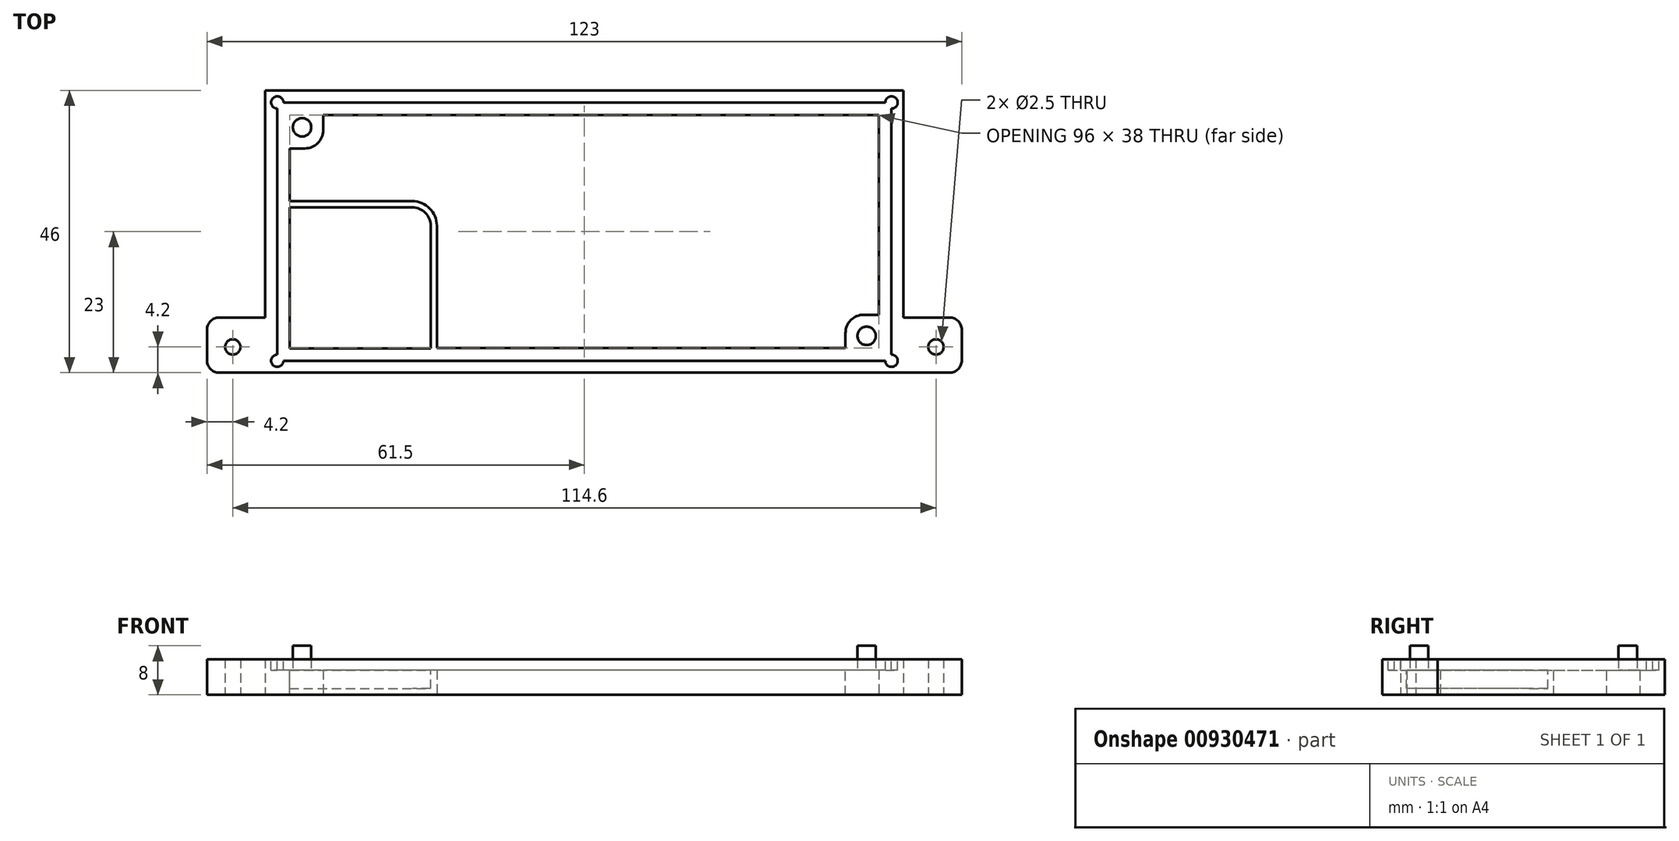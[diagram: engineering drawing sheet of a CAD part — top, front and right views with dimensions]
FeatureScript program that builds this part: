
annotation { "Feature Type Name" : "Feature", "Feature Type Description" : "" }
export const myFeature = defineFeature(function(context is Context, id is Id, definition is map)
    precondition{}
    {
        {
            var Q0;
            Q0=qCreatedBy(makeId("Top.planeOp"),FACE);
            var sketch = newSketch(context, id + "F0", { "sketchPlane" : qUnion([Q0])});
            skLineSegment(sketch, "E0.bottom", {"start": v(52, -23) * mm, "end": v(-52, -23) * mm});
            skLineSegment(sketch, "E0.top", {"start": v(52, 23) * mm, "end": v(-52, 23) * mm});
            skLineSegment(sketch, "E0.left", {"start": v(52, -23) * mm, "end": v(52, 23) * mm});
            skLineSegment(sketch, "E0.right", {"start": v(-52, -23) * mm, "end": v(-52, 23) * mm});
            skPoint(sketch, "E0.middle", {"position": v(0, 0) * mm});
            skSolve(sketch);
        }
        {
            var Q0;
            Q0 = qSketchRegion(id + "F0", true);
            extrude(context, id + "F1", {"entities" : qUnion([Q0]), "depth" : 5.8 * mm, "offsetDistance" : 25 * mm});
        }
        {
            var Q0;
            Q0=qCreatedBy(makeId("Top.planeOp"),FACE);
            var sketch = newSketch(context, id + "F2", { "sketchPlane" : qUnion([Q0])});
            skLineSegment(sketch, "E1.bottom", {"start": v(-61.5, -23) * mm, "end": v(61.5, -23) * mm});
            skLineSegment(sketch, "E1.top", {"start": v(-61.5, -14) * mm, "end": v(61.5, -14) * mm});
            skLineSegment(sketch, "E1.left", {"start": v(-61.5, -23) * mm, "end": v(-61.5, -14) * mm});
            skLineSegment(sketch, "E1.right", {"start": v(61.5, -23) * mm, "end": v(61.5, -14) * mm});
            skSolve(sketch);
        }
        {
            var Q0;
            Q0 = qSketchRegion(id + "F2", true);
            extrude(context, id + "F3", {"entities" : qUnion([Q0]), "operationType" : NewBodyOperationType.ADD, "depth" : 5.8 * mm, "offsetDistance" : 25 * mm});
        }
        {
            var Q0;
            Q0=qCreatedBy(makeId("Top.planeOp"),FACE);
            var sketch = newSketch(context, id + "F4", { "sketchPlane" : qUnion([Q0])});
            skCircle(sketch, "E2", {"center": v(-57.3, -18.8) * mm, "radius": 1.25 * mm});
            skSolve(sketch);
        }
        {
            var Q0;
            Q0 = qSketchRegion(id + "F4", true);
            extrude(context, id + "F5", {"entities" : qUnion([Q0]), "operationType" : NewBodyOperationType.REMOVE, "depth" : 5.8 * mm, "offsetDistance" : 25 * mm});
        }
        {
            var Q0;
            Q0=qCreatedBy(makeId("Top.planeOp"),FACE);
            var sketch = newSketch(context, id + "F6", { "sketchPlane" : qUnion([Q0])});
            skCircle(sketch, "E3", {"center": v(57.3, -18.8) * mm, "radius": 1.25 * mm});
            skSolve(sketch);
        }
        {
            var Q0;
            Q0 = qSketchRegion(id + "F6", true);
            extrude(context, id + "F7", {"entities" : qUnion([Q0]), "operationType" : NewBodyOperationType.REMOVE, "depth" : 5.8 * mm, "offsetDistance" : 25 * mm});
        }
        {
            var Q0;
            Q0=makeQuery(id+"F3.boolean.opBoolean","MERGE",FACE,{"derivedFrom":[makeQuery(id+"F1.opExtrude","CAP_FACE",FACE,{"disambiguationData":[OSD([sQuery(id+"F0.wireOp",EDGE,"E0.bottom"),sQuery(id+"F0.wireOp",EDGE,"E0.top"),sQuery(id+"F0.wireOp",EDGE,"E0.left"),sQuery(id+"F0.wireOp",EDGE,"E0.right")])],"isStart":false}),makeQuery(id+"F3.opExtrude","CAP_FACE",FACE,{"disambiguationData":[OSD([sQuery(id+"F2.wireOp",EDGE,"E1.bottom"),sQuery(id+"F2.wireOp",EDGE,"E1.top"),sQuery(id+"F2.wireOp",EDGE,"E1.left"),sQuery(id+"F2.wireOp",EDGE,"E1.right")])],"isStart":false})]});
            var sketch = newSketch(context, id + "F8", { "sketchPlane" : qUnion([Q0])});
            skLineSegment(sketch, "E4.bottom", {"start": v(50.05, -21.05) * mm, "end": v(-50.05, -21.05) * mm});
            skLineSegment(sketch, "E4.top", {"start": v(50.05, 21.05) * mm, "end": v(-50.05, 21.05) * mm});
            skLineSegment(sketch, "E4.left", {"start": v(50.05, -21.05) * mm, "end": v(50.05, 21.05) * mm});
            skLineSegment(sketch, "E4.right", {"start": v(-50.05, -21.05) * mm, "end": v(-50.05, 21.05) * mm});
            skPoint(sketch, "E4.middle", {"position": v(0, 0) * mm});
            skSolve(sketch);
        }
        {
            var Q0;
            Q0 = qSketchRegion(id + "F8", true);
            extrude(context, id + "F9", {"entities" : qUnion([Q0]), "operationType" : NewBodyOperationType.REMOVE, "oppositeDirection" : true, "depth" : 1.8 * mm, "offsetDistance" : 25 * mm});
        }
        {
            var Q0;
            Q0=makeQuery(id+"F9.boolean.opBoolean","COPY",FACE,{"derivedFrom":makeQuery(id+"F9.opExtrude","CAP_FACE",FACE,{"disambiguationData":[OSD([sQuery(id+"F8.wireOp",EDGE,"E4.bottom"),sQuery(id+"F8.wireOp",EDGE,"E4.top"),sQuery(id+"F8.wireOp",EDGE,"E4.left"),sQuery(id+"F8.wireOp",EDGE,"E4.right")])],"isStart":false})});
            var sketch = newSketch(context, id + "F10", { "sketchPlane" : qUnion([Q0])});
            skLineSegment(sketch, "E5.bottom", {"start": v(48, -19) * mm, "end": v(-48, -19) * mm});
            skLineSegment(sketch, "E5.top", {"start": v(48, 19) * mm, "end": v(-48, 19) * mm});
            skLineSegment(sketch, "E5.left", {"start": v(48, -19) * mm, "end": v(48, 19) * mm});
            skLineSegment(sketch, "E5.right", {"start": v(-48, -19) * mm, "end": v(-48, 19) * mm});
            skPoint(sketch, "E5.middle", {"position": v(0, 0) * mm});
            skSolve(sketch);
        }
        {
            var Q0;
            Q0 = qSketchRegion(id + "F10", true);
            extrude(context, id + "F11", {"entities" : qUnion([Q0]), "operationType" : NewBodyOperationType.REMOVE, "oppositeDirection" : true, "depth" : 4 * mm, "offsetDistance" : 25 * mm});
        }
        {
            var Q0;
            Q0=qCreatedBy(makeId("Top.planeOp"),FACE);
            var sketch = newSketch(context, id + "F12", { "sketchPlane" : qUnion([Q0])});
            skLineSegment(sketch, "E6.bottom", {"start": v(-50.05, 21.05) * mm, "end": v(-42.55, 21.05) * mm});
            skLineSegment(sketch, "E6.top", {"start": v(-50.05, 13.55) * mm, "end": v(-42.55, 13.55) * mm});
            skLineSegment(sketch, "E6.left", {"start": v(-50.05, 21.05) * mm, "end": v(-50.05, 13.55) * mm});
            skLineSegment(sketch, "E6.right", {"start": v(-42.55, 21.05) * mm, "end": v(-42.55, 13.55) * mm});
            skSolve(sketch);
        }
        {
            var Q0;
            Q0 = qSketchRegion(id + "F12", true);
            extrude(context, id + "F13", {"entities" : qUnion([Q0]), "operationType" : NewBodyOperationType.ADD, "depth" : 4 * mm, "offsetDistance" : 25 * mm});
        }
        {
            var Q0;
            Q0=qCreatedBy(makeId("Top.planeOp"),FACE);
            var sketch = newSketch(context, id + "F14", { "sketchPlane" : qUnion([Q0])});
            skLineSegment(sketch, "E7.bottom", {"start": v(50.05, -21.05) * mm, "end": v(42.55, -21.05) * mm});
            skLineSegment(sketch, "E7.top", {"start": v(50.05, -13.55) * mm, "end": v(42.55, -13.55) * mm});
            skLineSegment(sketch, "E7.left", {"start": v(50.05, -21.05) * mm, "end": v(50.05, -13.55) * mm});
            skLineSegment(sketch, "E7.right", {"start": v(42.55, -21.05) * mm, "end": v(42.55, -13.55) * mm});
            skSolve(sketch);
        }
        {
            var Q0;
            Q0 = qSketchRegion(id + "F14", true);
            extrude(context, id + "F15", {"entities" : qUnion([Q0]), "operationType" : NewBodyOperationType.ADD, "depth" : 4 * mm, "offsetDistance" : 25 * mm});
        }
        {
            var Q0;
            Q0=qCreatedBy(makeId("Top.planeOp"),FACE);
            var sketch = newSketch(context, id + "F16", { "sketchPlane" : qUnion([Q0])});
            skCircle(sketch, "E8", {"center": v(-46, 17) * mm, "radius": 1.5 * mm});
            skSolve(sketch);
        }
        {
            var Q0;
            Q0 = qSketchRegion(id + "F16", true);
            extrude(context, id + "F17", {"entities" : qUnion([Q0]), "operationType" : NewBodyOperationType.ADD, "depth" : 8 * mm, "offsetDistance" : 25 * mm});
        }
        {
            var Q0;
            Q0=qCreatedBy(makeId("Top.planeOp"),FACE);
            var sketch = newSketch(context, id + "F18", { "sketchPlane" : qUnion([Q0])});
            skCircle(sketch, "E9", {"center": v(46, -17) * mm, "radius": 1.5 * mm});
            skSolve(sketch);
        }
        {
            var Q0;
            Q0 = qSketchRegion(id + "F18", true);
            extrude(context, id + "F19", {"entities" : qUnion([Q0]), "operationType" : NewBodyOperationType.ADD, "depth" : 8 * mm, "offsetDistance" : 25 * mm});
        }
        {
            var Q0;
            Q0=qCreatedBy(makeId("Top.planeOp"),FACE);
            var sketch = newSketch(context, id + "F20", { "sketchPlane" : qUnion([Q0])});
            skLineSegment(sketch, "E10.bottom", {"start": v(-50.05, 4.95) * mm, "end": v(-24.05, 4.95) * mm});
            skLineSegment(sketch, "E10.top", {"start": v(-50.05, -21.05) * mm, "end": v(-24.05, -21.05) * mm});
            skLineSegment(sketch, "E10.left", {"start": v(-50.05, 4.95) * mm, "end": v(-50.05, -21.05) * mm});
            skLineSegment(sketch, "E10.right", {"start": v(-24.05, 4.95) * mm, "end": v(-24.05, -21.05) * mm});
            skSolve(sketch);
        }
        {
            var Q0;
            Q0 = qSketchRegion(id + "F20", true);
            extrude(context, id + "F21", {"entities" : qUnion([Q0]), "operationType" : NewBodyOperationType.ADD, "depth" : 4 * mm, "offsetDistance" : 25 * mm});
        }
        {
            var Q0;
            Q0=makeQuery(id+"F21.boolean.opBoolean","MERGE",FACE,{"derivedFrom":[makeQuery(id+"F15.boolean.opBoolean","MERGE",FACE,{"derivedFrom":[makeQuery(id+"F13.boolean.opBoolean","MERGE",FACE,{"derivedFrom":[makeQuery(id+"F9.boolean.opBoolean","COPY",FACE,{"derivedFrom":makeQuery(id+"F9.opExtrude","CAP_FACE",FACE,{"disambiguationData":[OSD([sQuery(id+"F8.wireOp",EDGE,"E4.bottom"),sQuery(id+"F8.wireOp",EDGE,"E4.top"),sQuery(id+"F8.wireOp",EDGE,"E4.left"),sQuery(id+"F8.wireOp",EDGE,"E4.right")])],"isStart":false})}),makeQuery(id+"F13.opExtrude","CAP_FACE",FACE,{"disambiguationData":[OSD([sQuery(id+"F12.wireOp",EDGE,"E6.bottom"),sQuery(id+"F12.wireOp",EDGE,"E6.top"),sQuery(id+"F12.wireOp",EDGE,"E6.left"),sQuery(id+"F12.wireOp",EDGE,"E6.right")])],"isStart":false})]}),makeQuery(id+"F15.opExtrude","CAP_FACE",FACE,{"disambiguationData":[OSD([sQuery(id+"F14.wireOp",EDGE,"E7.bottom"),sQuery(id+"F14.wireOp",EDGE,"E7.top"),sQuery(id+"F14.wireOp",EDGE,"E7.left"),sQuery(id+"F14.wireOp",EDGE,"E7.right")])],"isStart":false})]}),makeQuery(id+"F21.opExtrude","CAP_FACE",FACE,{"disambiguationData":[OSD([sQuery(id+"F20.wireOp",EDGE,"E10.bottom"),sQuery(id+"F20.wireOp",EDGE,"E10.top"),sQuery(id+"F20.wireOp",EDGE,"E10.left"),sQuery(id+"F20.wireOp",EDGE,"E10.right")])],"isStart":false})]});
            var sketch = newSketch(context, id + "F22", { "sketchPlane" : qUnion([Q0])});
            skLineSegment(sketch, "E11.bottom", {"start": v(-48.05, 3.95) * mm, "end": v(-25.05, 3.95) * mm});
            skLineSegment(sketch, "E11.top", {"start": v(-48.05, -19.05) * mm, "end": v(-25.05, -19.05) * mm});
            skLineSegment(sketch, "E11.left", {"start": v(-48.05, 3.95) * mm, "end": v(-48.05, -19.05) * mm});
            skLineSegment(sketch, "E11.right", {"start": v(-25.05, 3.95) * mm, "end": v(-25.05, -19.05) * mm});
            skSolve(sketch);
        }
        {
            var Q0;
            Q0 = qSketchRegion(id + "F22", true);
            extrude(context, id + "F23", {"entities" : qUnion([Q0]), "operationType" : NewBodyOperationType.REMOVE, "oppositeDirection" : true, "depth" : 3 * mm, "offsetDistance" : 25 * mm});
        }
        {
            var Q0;
            Q0=makeQuery(id+"F23.boolean.opBoolean","COPY",EDGE,{"derivedFrom":makeQuery(id+"F23.opExtrude","SWEPT_EDGE",EDGE,{"disambiguationData":[OSD([sQuery(id+"F22.wireOp",EDGE,"E11.bottom"),sQuery(id+"F22.wireOp",EDGE,"E11.right")])]})});
            fillet(context, id + "F24", {"entities" : qUnion([Q0]), "radius" : 3 * mm, "tangentPropagation" : true, "allowEdgeOverflow" : false});
        }
        {
            var Q0;
            Q0=makeQuery(id+"F21.opExtrude","SWEPT_EDGE",EDGE,{"disambiguationData":[OSD([sQuery(id+"F20.wireOp",EDGE,"E10.bottom"),sQuery(id+"F20.wireOp",EDGE,"E10.right")])]});
            fillet(context, id + "F25", {"entities" : qUnion([Q0]), "radius" : 4 * mm, "tangentPropagation" : true, "allowEdgeOverflow" : false});
        }
        {
            var Q0;
            Q0=makeQuery(id+"F13.opExtrude","SWEPT_EDGE",EDGE,{"disambiguationData":[OSD([sQuery(id+"F12.wireOp",EDGE,"E6.top"),sQuery(id+"F12.wireOp",EDGE,"E6.right")])]});
            fillet(context, id + "F26", {"entities" : qUnion([Q0]), "radius" : 3 * mm, "tangentPropagation" : true, "allowEdgeOverflow" : false});
        }
        {
            var Q0;
            Q0=makeQuery(id+"F15.opExtrude","SWEPT_EDGE",EDGE,{"disambiguationData":[OSD([sQuery(id+"F14.wireOp",EDGE,"E7.top"),sQuery(id+"F14.wireOp",EDGE,"E7.right")])]});
            fillet(context, id + "F27", {"entities" : qUnion([Q0]), "radius" : 3 * mm, "tangentPropagation" : true, "allowEdgeOverflow" : false});
        }
        {
            var Q0;
            Q0=makeQuery(id+"F3.opExtrude","SWEPT_EDGE",EDGE,{"disambiguationData":[OSD([sQuery(id+"F2.wireOp",EDGE,"E1.top"),sQuery(id+"F2.wireOp",EDGE,"E1.left")])]});
            var Q1;
            Q1=makeQuery(id+"F3.opExtrude","SWEPT_EDGE",EDGE,{"disambiguationData":[OSD([sQuery(id+"F2.wireOp",EDGE,"E1.bottom"),sQuery(id+"F2.wireOp",EDGE,"E1.left")])]});
            var Q2;
            Q2=makeQuery(id+"F3.opExtrude","SWEPT_EDGE",EDGE,{"disambiguationData":[OSD([sQuery(id+"F2.wireOp",EDGE,"E1.bottom"),sQuery(id+"F2.wireOp",EDGE,"E1.right")])]});
            var Q3;
            Q3=makeQuery(id+"F3.opExtrude","SWEPT_EDGE",EDGE,{"disambiguationData":[OSD([sQuery(id+"F2.wireOp",EDGE,"E1.top"),sQuery(id+"F2.wireOp",EDGE,"E1.right")])]});
            fillet(context, id + "F28", {"entities" : qUnion([Q0, Q1, Q2, Q3]), "radius" : 2 * mm, "tangentPropagation" : true, "allowEdgeOverflow" : false});
        }
        {
            var Q0;
            Q0=makeQuery(id+"F3.boolean.opBoolean","MERGE",FACE,{"derivedFrom":[makeQuery(id+"F1.opExtrude","CAP_FACE",FACE,{"disambiguationData":[OSD([sQuery(id+"F0.wireOp",EDGE,"E0.bottom"),sQuery(id+"F0.wireOp",EDGE,"E0.top"),sQuery(id+"F0.wireOp",EDGE,"E0.left"),sQuery(id+"F0.wireOp",EDGE,"E0.right")])],"isStart":false}),makeQuery(id+"F3.opExtrude","CAP_FACE",FACE,{"disambiguationData":[OSD([sQuery(id+"F2.wireOp",EDGE,"E1.bottom"),sQuery(id+"F2.wireOp",EDGE,"E1.top"),sQuery(id+"F2.wireOp",EDGE,"E1.left"),sQuery(id+"F2.wireOp",EDGE,"E1.right")])],"isStart":false})]});
            var sketch = newSketch(context, id + "F29", { "sketchPlane" : qUnion([Q0])});
            skCircle(sketch, "E12", {"center": v(-50.05, 21.05) * mm, "radius": 1 * mm});
            skSolve(sketch);
        }
        {
            var Q0;
            Q0 = qSketchRegion(id + "F29", true);
            extrude(context, id + "F30", {"entities" : qUnion([Q0]), "operationType" : NewBodyOperationType.REMOVE, "oppositeDirection" : true, "depth" : 1.8 * mm, "offsetDistance" : 25 * mm});
        }
        {
            var Q0;
            Q0=makeQuery(id+"F3.boolean.opBoolean","MERGE",FACE,{"derivedFrom":[makeQuery(id+"F1.opExtrude","CAP_FACE",FACE,{"disambiguationData":[OSD([sQuery(id+"F0.wireOp",EDGE,"E0.bottom"),sQuery(id+"F0.wireOp",EDGE,"E0.top"),sQuery(id+"F0.wireOp",EDGE,"E0.left"),sQuery(id+"F0.wireOp",EDGE,"E0.right")])],"isStart":false}),makeQuery(id+"F3.opExtrude","CAP_FACE",FACE,{"disambiguationData":[OSD([sQuery(id+"F2.wireOp",EDGE,"E1.bottom"),sQuery(id+"F2.wireOp",EDGE,"E1.top"),sQuery(id+"F2.wireOp",EDGE,"E1.left"),sQuery(id+"F2.wireOp",EDGE,"E1.right")])],"isStart":false})]});
            var sketch = newSketch(context, id + "F31", { "sketchPlane" : qUnion([Q0])});
            skCircle(sketch, "E13", {"center": v(-50.05, -21.05) * mm, "radius": 1 * mm});
            skSolve(sketch);
        }
        {
            var Q0;
            Q0 = qSketchRegion(id + "F31", true);
            extrude(context, id + "F32", {"entities" : qUnion([Q0]), "operationType" : NewBodyOperationType.REMOVE, "oppositeDirection" : true, "depth" : 1.8 * mm, "offsetDistance" : 25 * mm});
        }
        {
            var Q0;
            Q0=makeQuery(id+"F3.boolean.opBoolean","MERGE",FACE,{"derivedFrom":[makeQuery(id+"F1.opExtrude","CAP_FACE",FACE,{"disambiguationData":[OSD([sQuery(id+"F0.wireOp",EDGE,"E0.bottom"),sQuery(id+"F0.wireOp",EDGE,"E0.top"),sQuery(id+"F0.wireOp",EDGE,"E0.left"),sQuery(id+"F0.wireOp",EDGE,"E0.right")])],"isStart":false}),makeQuery(id+"F3.opExtrude","CAP_FACE",FACE,{"disambiguationData":[OSD([sQuery(id+"F2.wireOp",EDGE,"E1.bottom"),sQuery(id+"F2.wireOp",EDGE,"E1.top"),sQuery(id+"F2.wireOp",EDGE,"E1.left"),sQuery(id+"F2.wireOp",EDGE,"E1.right")])],"isStart":false})]});
            var sketch = newSketch(context, id + "F33", { "sketchPlane" : qUnion([Q0])});
            skCircle(sketch, "E14", {"center": v(50.05, -21.05) * mm, "radius": 1 * mm});
            skCircle(sketch, "E15", {"center": v(50.05, 21.05) * mm, "radius": 1 * mm});
            skSolve(sketch);
        }
        {
            var Q0;
            Q0 = qSketchRegion(id + "F33", true);
            extrude(context, id + "F34", {"entities" : qUnion([Q0]), "operationType" : NewBodyOperationType.REMOVE, "oppositeDirection" : true, "depth" : 1.8 * mm, "offsetDistance" : 25 * mm});
        }
    });
